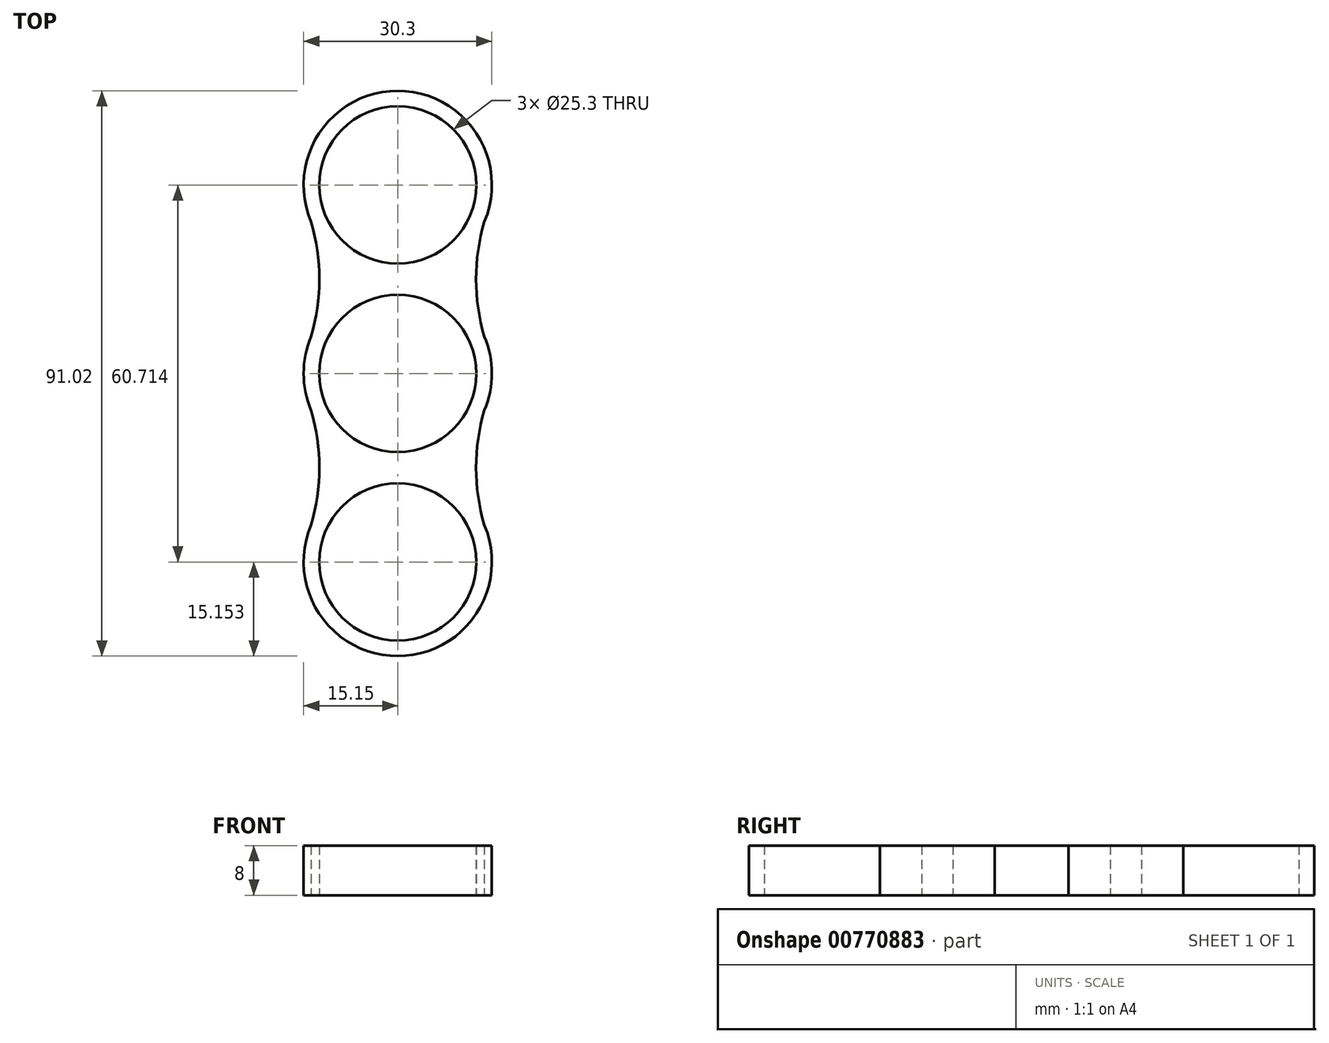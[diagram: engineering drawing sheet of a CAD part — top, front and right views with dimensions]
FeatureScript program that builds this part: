
annotation { "Feature Type Name" : "Feature", "Feature Type Description" : "" }
export const myFeature = defineFeature(function(context is Context, id is Id, definition is map)
    precondition{}
    {
        {
            var Q0;
            Q0=qCreatedBy(makeId("Top.planeOp"),FACE);
            var sketch = newSketch(context, id + "F0", { "sketchPlane" : qUnion([Q0])});
            skCircle(sketch, "E0", {"center": v(0, 0) * mm, "radius": 12.65 * mm});
            skArc(sketch, "E1", {"start": v(13.94, -5.93) * mm, "mid": v(15.15, 0) * mm, "end": v(13.94, 5.93) * mm});
            skCircle(sketch, "E2", {"center": v(0, 30.36) * mm, "radius": 12.65 * mm});
            skArc(sketch, "E3", {"start": v(13.94, 24.43) * mm, "mid": v(0, 45.5) * mm, "end": v(-13.94, 24.43) * mm});
            skArc(sketch, "E4", {"start": v(-13.94, 5.93) * mm, "mid": v(-12.61, 15.18) * mm, "end": v(-13.94, 24.43) * mm});
            skPoint(sketch, "E5.orphan", {"position": v(-15.15, 30.36) * mm});
            skPoint(sketch, "E6.start.orphan", {"position": v(-15.15, 0) * mm});
            skPoint(sketch, "E7.start.orphan", {"position": v(-15.15, 15.18) * mm});
            skArc(sketch, "E8.MirrorCS", {"start": v(13.94, 5.93) * mm, "mid": v(12.61, 15.18) * mm, "end": v(13.94, 24.43) * mm});
            skArc(sketch, "E9.1.0", {"start": v(13.94, -5.93) * mm, "mid": v(12.61, -15.18) * mm, "end": v(13.94, -24.43) * mm});
            skArc(sketch, "E9.1.1", {"start": v(-13.94, -24.43) * mm, "mid": v(0, -45.5) * mm, "end": v(13.94, -24.43) * mm});
            skCircle(sketch, "E9.1.2", {"center": v(0, -30.36) * mm, "radius": 12.65 * mm});
            skArc(sketch, "E9.1.3", {"start": v(-13.94, -5.93) * mm, "mid": v(-12.61, -15.18) * mm, "end": v(-13.94, -24.43) * mm});
            skArc(sketch, "E10.trimOffspring", {"start": v(-13.94, 5.93) * mm, "mid": v(-15.15, 0) * mm, "end": v(-13.94, -5.93) * mm});
            skSolve(sketch);
        }
        {
            var Q0;
            Q0=makeQuery(id+"F0.imprint","IMPRINT",FACE,{"disambiguationData":[TD([[makeQuery(id+"F0.imprint","IMPRINT",EDGE,{"derivedFrom":sQuery(id+"F0.wireOp",EDGE,"E0")}),-1.0]])]});
            extrude(context, id + "F1", {"entities" : qUnion([Q0]), "depth" : 8 * mm, "offsetDistance" : 25 * mm});
        }
    });
